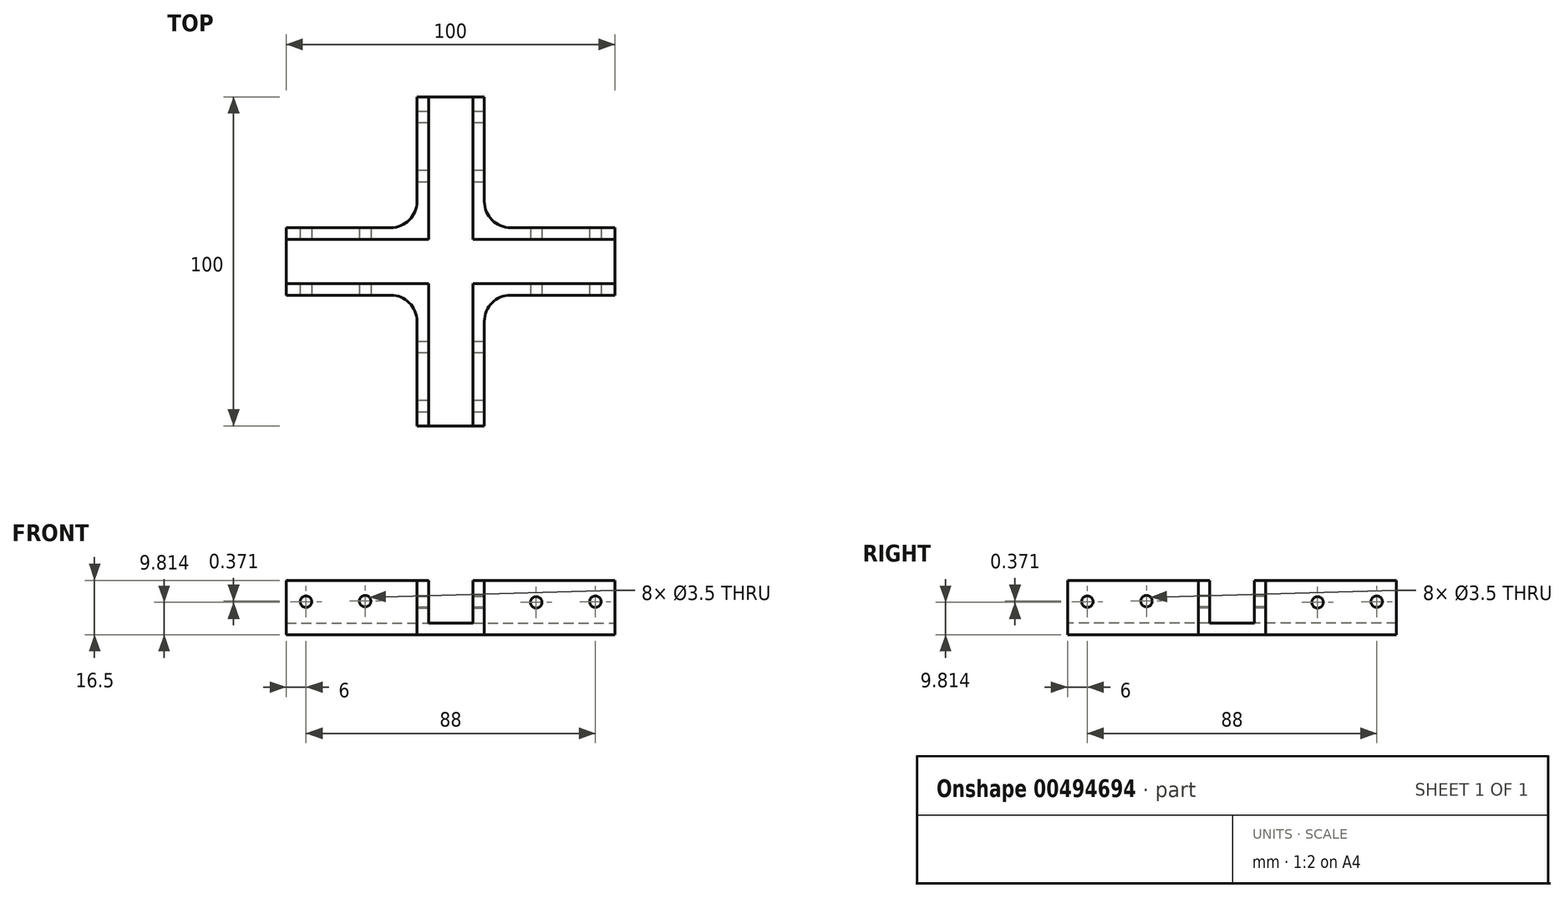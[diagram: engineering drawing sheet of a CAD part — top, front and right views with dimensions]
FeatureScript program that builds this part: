
annotation { "Feature Type Name" : "Feature", "Feature Type Description" : "" }
export const myFeature = defineFeature(function(context is Context, id is Id, definition is map)
    precondition{}
    {
        {
            var Q0;
            Q0=qCreatedBy(makeId("Top.planeOp"),FACE);
            var sketch = newSketch(context, id + "F0", { "sketchPlane" : qUnion([Q0])});
            skLineSegment(sketch, "E0.bottom", {"start": v(-50, 10.25) * mm, "end": v(-10.25, 10.25) * mm});
            skLineSegment(sketch, "E0.top", {"start": v(-50, -10.25) * mm, "end": v(-10.25, -10.25) * mm});
            skLineSegment(sketch, "E0.left", {"start": v(-50, 10.25) * mm, "end": v(-50, -10.25) * mm});
            skLineSegment(sketch, "E0.right", {"start": v(50, 10.25) * mm, "end": v(50, -10.25) * mm});
            skPoint(sketch, "E1", {"position": v(0, 10.25) * mm});
            skPoint(sketch, "E2", {"position": v(50, 0) * mm});
            skLineSegment(sketch, "E3.bottom", {"start": v(-10.25, -50) * mm, "end": v(-10.25, -10.25) * mm});
            skLineSegment(sketch, "E3.top", {"start": v(10.25, -50) * mm, "end": v(10.25, -10.25) * mm});
            skLineSegment(sketch, "E3.left", {"start": v(-10.25, -50) * mm, "end": v(10.25, -50) * mm});
            skLineSegment(sketch, "E3.right", {"start": v(-10.25, 50) * mm, "end": v(10.25, 50) * mm});
            skPoint(sketch, "E4", {"position": v(-10.25, 0) * mm});
            skPoint(sketch, "E5", {"position": v(0, 50) * mm});
            skLineSegment(sketch, "E6.trimOffspring", {"start": v(10.25, 10.25) * mm, "end": v(10.25, 50) * mm});
            skLineSegment(sketch, "E7.trimOffspring", {"start": v(10.25, -10.25) * mm, "end": v(50, -10.25) * mm});
            skLineSegment(sketch, "E8.trimOffspring", {"start": v(-10.25, 10.25) * mm, "end": v(-10.25, 50) * mm});
            skLineSegment(sketch, "E9.trimOffspring", {"start": v(10.25, 10.25) * mm, "end": v(50, 10.25) * mm});
            skSolve(sketch);
        }
        {
            var Q0;
            Q0 = qSketchRegion(id + "F0", true);
            extrude(context, id + "F1", {"entities" : qUnion([Q0]), "depth" : 16.5 * mm, "offsetDistance" : 25 * mm});
        }
        {
            var Q0;
            Q0=makeQuery(id+"F1.opExtrude","SWEPT_FACE",FACE,{"disambiguationData":[OSD([sQuery(id+"F0.wireOp",EDGE,"E3.left")])]});
            var sketch = newSketch(context, id + "F2", { "sketchPlane" : qUnion([Q0])});
            skLineSegment(sketch, "E10.top", {"start": v(-6.75, 3.5) * mm, "end": v(6.75, 3.5) * mm});
            skLineSegment(sketch, "E10.left", {"start": v(-6.75, 16.5) * mm, "end": v(-6.75, 3.5) * mm});
            skLineSegment(sketch, "E10.right", {"start": v(6.75, 16.5) * mm, "end": v(6.75, 3.5) * mm});
            skPoint(sketch, "E11", {"position": v(0, 3.5) * mm});
            skLineSegment(sketch, "E12", {"start": v(-6.75, 16.5) * mm, "end": v(6.75, 16.5) * mm});
            skSolve(sketch);
        }
        {
            var Q0;
            Q0 = qSketchRegion(id + "F2", true);
            extrude(context, id + "F3", {"entities" : qUnion([Q0]), "operationType" : NewBodyOperationType.REMOVE, "endBound" : BoundingType.THROUGH_ALL, "oppositeDirection" : true, "depth" : 25 * mm, "offsetDistance" : 25 * mm});
        }
        {
            var Q0;
            Q0=makeQuery(id+"F1.opExtrude","SWEPT_FACE",FACE,{"disambiguationData":[OSD([sQuery(id+"F0.wireOp",EDGE,"E0.right")])]});
            var sketch = newSketch(context, id + "F4", { "sketchPlane" : qUnion([Q0])});
            skLineSegment(sketch, "E13.top", {"start": v(-6.75, 3.5) * mm, "end": v(6.75, 3.5) * mm});
            skLineSegment(sketch, "E13.left", {"start": v(-6.75, 16.5) * mm, "end": v(-6.75, 3.5) * mm});
            skLineSegment(sketch, "E13.right", {"start": v(6.75, 16.5) * mm, "end": v(6.75, 3.5) * mm});
            skPoint(sketch, "E14", {"position": v(0, 3.5) * mm});
            skLineSegment(sketch, "E15", {"start": v(-6.75, 16.5) * mm, "end": v(6.75, 16.5) * mm});
            skSolve(sketch);
        }
        {
            var Q0;
            Q0 = qSketchRegion(id + "F4", true);
            extrude(context, id + "F5", {"entities" : qUnion([Q0]), "operationType" : NewBodyOperationType.REMOVE, "endBound" : BoundingType.THROUGH_ALL, "oppositeDirection" : true, "depth" : 25 * mm});
        }
        {
            var Q0;
            Q0=makeQuery(id+"F1.opExtrude","SWEPT_FACE",FACE,{"disambiguationData":[OSD([sQuery(id+"F0.wireOp",EDGE,"E7.trimOffspring")])]});
            var sketch = newSketch(context, id + "F6", { "sketchPlane" : qUnion([Q0])});
            skCircle(sketch, "E16", {"center": v(44, 10) * mm, "radius": 1.75 * mm});
            skCircle(sketch, "E17.1.0.0", {"center": v(26, 9.81) * mm, "radius": 1.75 * mm});
            skLineSegment(sketch, "E17.direction1", {"start": v(44, 10) * mm, "end": v(26, 9.81) * mm, "construction": true});
            skCircle(sketch, "E18", {"center": v(-26, 10.19) * mm, "radius": 1.75 * mm});
            skCircle(sketch, "E19.1.0.0", {"center": v(-44, 10) * mm, "radius": 1.75 * mm});
            skLineSegment(sketch, "E19.direction1", {"start": v(-26, 10.19) * mm, "end": v(-44, 10) * mm, "construction": true});
            skSolve(sketch);
        }
        {
            var Q0;
            Q0 = qSketchRegion(id + "F6", true);
            extrude(context, id + "F7", {"entities" : qUnion([Q0]), "operationType" : NewBodyOperationType.REMOVE, "endBound" : BoundingType.THROUGH_ALL, "oppositeDirection" : true, "depth" : 25 * mm});
        }
        {
            var Q0;
            Q0=makeQuery(id+"F1.opExtrude","SWEPT_FACE",FACE,{"disambiguationData":[OSD([sQuery(id+"F0.wireOp",EDGE,"E6.trimOffspring")])]});
            var sketch = newSketch(context, id + "F8", { "sketchPlane" : qUnion([Q0])});
            skCircle(sketch, "E20", {"center": v(44, 10) * mm, "radius": 1.75 * mm});
            skCircle(sketch, "E21.1.0.0", {"center": v(26, 9.81) * mm, "radius": 1.75 * mm});
            skLineSegment(sketch, "E21.direction1", {"start": v(44, 10) * mm, "end": v(26, 9.81) * mm, "construction": true});
            skCircle(sketch, "E22", {"center": v(-26, 10.19) * mm, "radius": 1.75 * mm});
            skCircle(sketch, "E23.1.0.0", {"center": v(-44, 10) * mm, "radius": 1.75 * mm});
            skLineSegment(sketch, "E23.direction1", {"start": v(-26, 10.19) * mm, "end": v(-44, 10) * mm, "construction": true});
            skSolve(sketch);
        }
        {
            var Q0;
            Q0 = qSketchRegion(id + "F8", true);
            extrude(context, id + "F9", {"entities" : qUnion([Q0]), "operationType" : NewBodyOperationType.REMOVE, "endBound" : BoundingType.THROUGH_ALL, "oppositeDirection" : true, "depth" : 25 * mm});
        }
        {
            var Q0;
            Q0=makeQuery(id+"F1.opExtrude","SWEPT_EDGE",EDGE,{"disambiguationData":[OSD([sQuery(id+"F0.wireOp",EDGE,"E3.top"),sQuery(id+"F0.wireOp",EDGE,"E7.trimOffspring")])]});
            var Q1;
            Q1=makeQuery(id+"F1.opExtrude","SWEPT_EDGE",EDGE,{"disambiguationData":[OSD([sQuery(id+"F0.wireOp",EDGE,"E6.trimOffspring"),sQuery(id+"F0.wireOp",EDGE,"E9.trimOffspring")])]});
            var Q2;
            Q2=makeQuery(id+"F1.opExtrude","SWEPT_EDGE",EDGE,{"disambiguationData":[OSD([sQuery(id+"F0.wireOp",EDGE,"E0.bottom"),sQuery(id+"F0.wireOp",EDGE,"E8.trimOffspring")])]});
            var Q3;
            Q3=makeQuery(id+"F1.opExtrude","SWEPT_EDGE",EDGE,{"disambiguationData":[OSD([sQuery(id+"F0.wireOp",EDGE,"E0.top"),sQuery(id+"F0.wireOp",EDGE,"E3.bottom")])]});
            fillet(context, id + "F10", {"entities" : qUnion([Q0, Q1, Q2, Q3]), "radius" : 8 * mm, "tangentPropagation" : true, "allowEdgeOverflow" : false});
        }
    });
